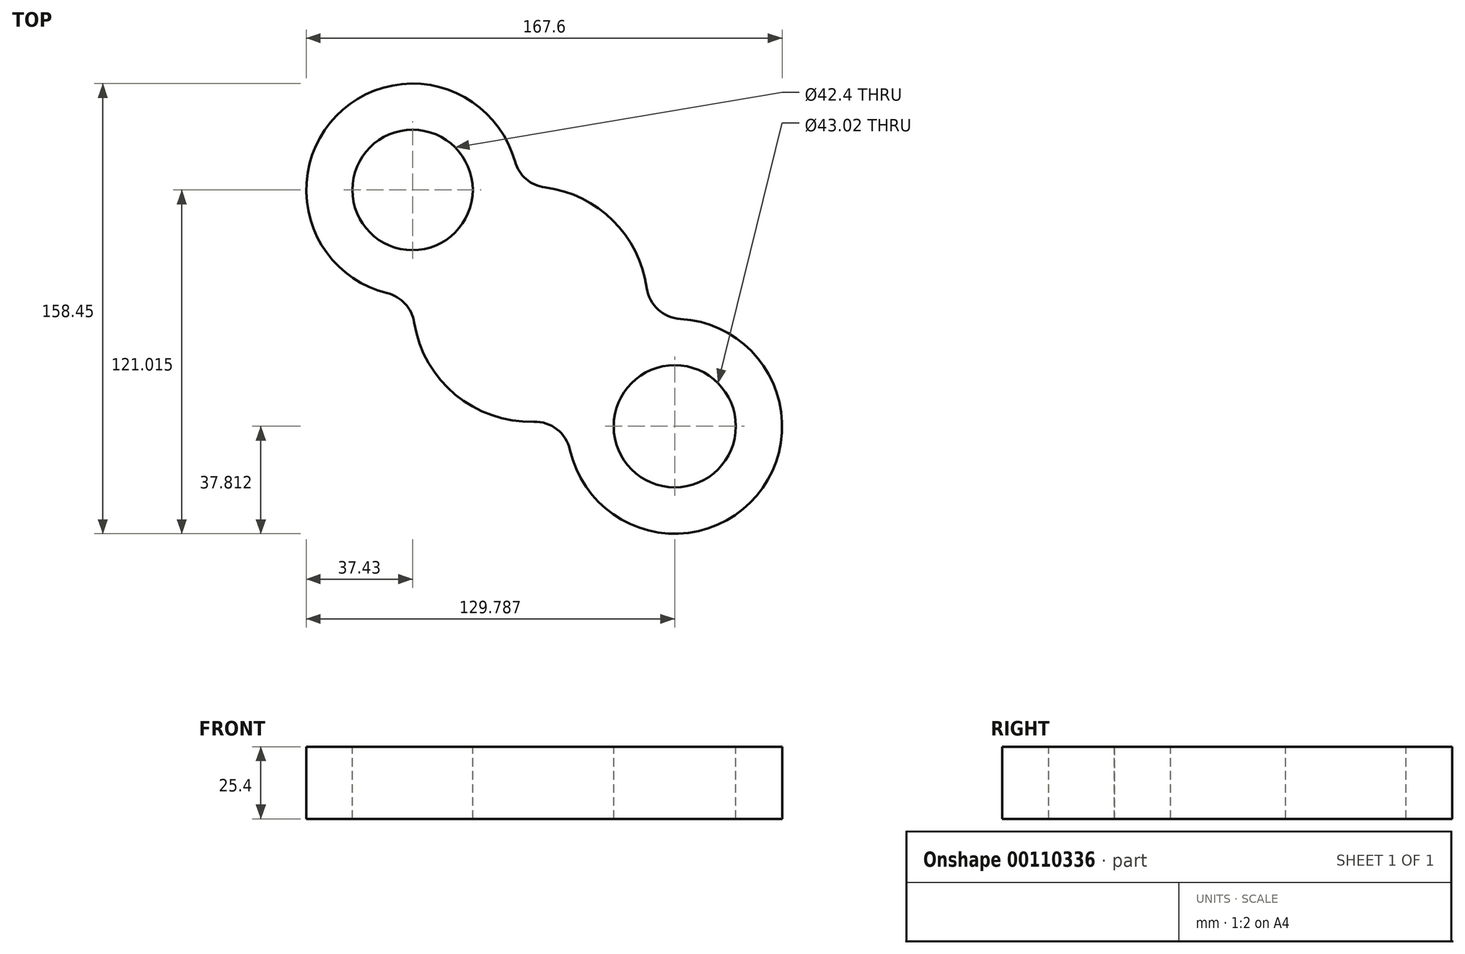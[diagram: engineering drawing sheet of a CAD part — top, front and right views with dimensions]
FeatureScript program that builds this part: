
annotation { "Feature Type Name" : "Feature", "Feature Type Description" : "" }
export const myFeature = defineFeature(function(context is Context, id is Id, definition is map)
    precondition{}
    {
        {
            var Q0;
            Q0=qCreatedBy(makeId("Top.planeOp"),FACE);
            var sketch = newSketch(context, id + "F0", { "sketchPlane" : qUnion([Q0])});
            skArc(sketch, "E0", {"start": v(-20.84, 47.01) * mm, "mid": v(-85.14, 72.08) * mm, "end": v(-58.07, 8.6) * mm});
            skArc(sketch, "E1", {"start": v(-58.07, 8.6) * mm, "mid": v(-42.03, -26.99) * mm, "end": v(-3.53, -33.41) * mm});
            skArc(sketch, "E2", {"start": v(-3.53, -33.41) * mm, "mid": v(62.98, -61.6) * mm, "end": v(24.12, -0.7) * mm});
            skArc(sketch, "E3.trimOffspring", {"start": v(24.12, -0.7) * mm, "mid": v(13.37, 34.2) * mm, "end": v(-20.84, 47.01) * mm});
            skSolve(sketch);
        }
        {
            var Q0;
            Q0=makeQuery(id+"F0.imprint","IMPRINT",FACE,{"disambiguationData":[TD([[makeQuery(id+"F0.imprint","IMPRINT",EDGE,{"derivedFrom":sQuery(id+"F0.wireOp",EDGE,"E0")}),1.0]])]});
            extrude(context, id + "F1", {"entities" : qUnion([Q0]), "depth" : 25.4 * mm});
        }
        {
            var Q0;
            Q0=makeQuery(id+"F1.opExtrude","CAP_FACE",FACE,{"disambiguationData":[OSD([sQuery(id+"F0.wireOp",EDGE,"E0"),sQuery(id+"F0.wireOp",EDGE,"E1"),sQuery(id+"F0.wireOp",EDGE,"E2"),sQuery(id+"F0.wireOp",EDGE,"E3.trimOffspring")])],"isStart":false});
            var sketch = newSketch(context, id + "F2", { "sketchPlane" : qUnion([Q0])});
            skCircle(sketch, "E4", {"center": v(-58.26, 46.03) * mm, "radius": 21.2 * mm});
            skSolve(sketch);
        }
        {
            var Q0;
            Q0=makeQuery(id+"F2.imprint","IMPRINT",FACE,{"disambiguationData":[TD([[makeQuery(id+"F2.imprint","IMPRINT",EDGE,{"derivedFrom":sQuery(id+"F2.wireOp",EDGE,"E4")}),1.0]])]});
            var Q1;
            Q1=sQuery(id+"F2.wireOp",EDGE,"E4");
            extrude(context, id + "F3", {"entities" : qUnion([Q0]), "operationType" : NewBodyOperationType.REMOVE, "surfaceEntities" : qUnion([Q1]), "endBound" : BoundingType.THROUGH_ALL, "oppositeDirection" : true, "depth" : 25.4 * mm});
        }
        {
            var Q0;
            Q0=makeQuery(id+"F1.opExtrude","SWEPT_EDGE",EDGE,{"disambiguationData":[OSD([sQuery(id+"F0.wireOp",EDGE,"E1"),sQuery(id+"F0.wireOp",EDGE,"E2")])]});
            fillet(context, id + "F4", {"entities" : qUnion([Q0]), "radius" : 12.7 * mm, "tangentPropagation" : true, "allowEdgeOverflow" : false});
        }
        {
            var Q0;
            Q0=makeQuery(id+"F1.opExtrude","SWEPT_EDGE",EDGE,{"disambiguationData":[OSD([sQuery(id+"F0.wireOp",EDGE,"E2"),sQuery(id+"F0.wireOp",EDGE,"E3.trimOffspring")])]});
            fillet(context, id + "F5", {"entities" : qUnion([Q0]), "radius" : 12.7 * mm, "tangentPropagation" : true, "allowEdgeOverflow" : false});
        }
        {
            var Q0;
            Q0=makeQuery(id+"F1.opExtrude","SWEPT_EDGE",EDGE,{"disambiguationData":[OSD([sQuery(id+"F0.wireOp",EDGE,"E0"),sQuery(id+"F0.wireOp",EDGE,"E3.trimOffspring")])]});
            fillet(context, id + "F6", {"entities" : qUnion([Q0]), "radius" : 12.7 * mm, "tangentPropagation" : true, "allowEdgeOverflow" : false});
        }
        {
            var Q0;
            Q0=makeQuery(id+"F1.opExtrude","SWEPT_EDGE",EDGE,{"disambiguationData":[OSD([sQuery(id+"F0.wireOp",EDGE,"E0"),sQuery(id+"F0.wireOp",EDGE,"E1")])]});
            fillet(context, id + "F7", {"entities" : qUnion([Q0]), "radius" : 12.7 * mm, "tangentPropagation" : true, "allowEdgeOverflow" : false});
        }
        {
            var Q0;
            Q0=makeQuery(id+"F1.opExtrude","CAP_FACE",FACE,{"disambiguationData":[OSD([sQuery(id+"F0.wireOp",EDGE,"E0"),sQuery(id+"F0.wireOp",EDGE,"E1"),sQuery(id+"F0.wireOp",EDGE,"E2"),sQuery(id+"F0.wireOp",EDGE,"E3.trimOffspring")])],"isStart":false});
            var sketch = newSketch(context, id + "F8", { "sketchPlane" : qUnion([Q0])});
            skCircle(sketch, "E5", {"center": v(34.1, -37.18) * mm, "radius": 21.5 * mm});
            skSolve(sketch);
        }
        {
            var Q0;
            Q0=makeQuery(id+"F8.imprint","IMPRINT",FACE,{"disambiguationData":[TD([[makeQuery(id+"F8.imprint","IMPRINT",EDGE,{"derivedFrom":sQuery(id+"F8.wireOp",EDGE,"E5")}),1.0]])]});
            var Q1;
            Q1=sQuery(id+"F8.wireOp",EDGE,"E5");
            extrude(context, id + "F9", {"entities" : qUnion([Q0]), "operationType" : NewBodyOperationType.REMOVE, "surfaceEntities" : qUnion([Q1]), "endBound" : BoundingType.THROUGH_ALL, "oppositeDirection" : true, "depth" : 25.4 * mm});
        }
    });
